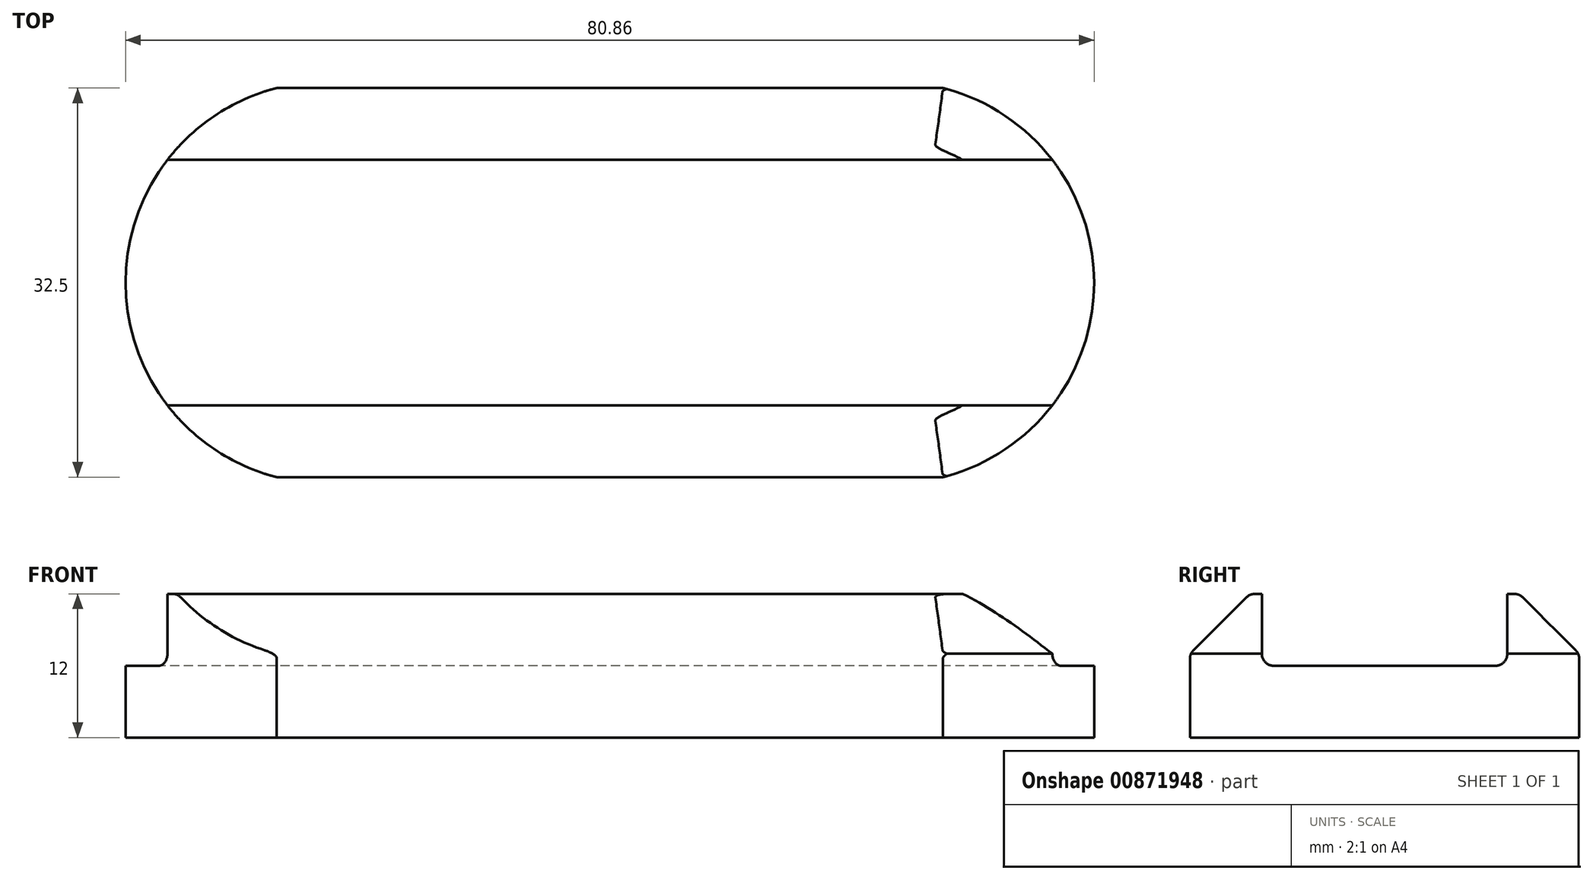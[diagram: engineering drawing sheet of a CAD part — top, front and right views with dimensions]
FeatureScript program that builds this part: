
annotation { "Feature Type Name" : "Feature", "Feature Type Description" : "" }
export const myFeature = defineFeature(function(context is Context, id is Id, definition is map)
    precondition{}
    {
        {
            var Q0;
            Q0=qCreatedBy(makeId("Top.planeOp"),FACE);
            var sketch = newSketch(context, id + "F0", { "sketchPlane" : qUnion([Q0])});
            skLineSegment(sketch, "E0", {"start": v(-30.41, 0) * mm, "end": v(25.96, 0) * mm, "construction": true});
            skLineSegment(sketch, "E1", {"start": v(0, 29.47) * mm, "end": v(0, -28.8) * mm, "construction": true});
            skLineSegment(sketch, "E2.bottom", {"start": v(-36.94, 10.25) * mm, "end": v(36.94, 10.25) * mm});
            skLineSegment(sketch, "E2.top", {"start": v(-36.94, -10.25) * mm, "end": v(36.94, -10.25) * mm});
            skLineSegment(sketch, "E2.left", {"start": v(-27.8, 10.25) * mm, "end": v(-27.8, -10.25) * mm});
            skLineSegment(sketch, "E2.right", {"start": v(27.8, 10.25) * mm, "end": v(27.8, -10.25) * mm});
            skLineSegment(sketch, "E3.bottom", {"start": v(-27.8, 10.25) * mm, "end": v(27.8, 10.25) * mm});
            skLineSegment(sketch, "E3.top", {"start": v(-27.8, 16.25) * mm, "end": v(27.8, 16.25) * mm});
            skLineSegment(sketch, "E3.left", {"start": v(-27.8, 10.25) * mm, "end": v(-27.8, 16.25) * mm});
            skLineSegment(sketch, "E3.right", {"start": v(27.8, 10.25) * mm, "end": v(27.8, 16.25) * mm});
            skLineSegment(sketch, "E4.bottom", {"start": v(-27.8, -10.25) * mm, "end": v(27.8, -10.25) * mm});
            skLineSegment(sketch, "E4.top", {"start": v(-27.8, -16.25) * mm, "end": v(27.8, -16.25) * mm});
            skLineSegment(sketch, "E4.left", {"start": v(-27.8, -10.25) * mm, "end": v(-27.8, -16.25) * mm});
            skLineSegment(sketch, "E4.right", {"start": v(27.8, -10.25) * mm, "end": v(27.8, -16.25) * mm});
            skArc(sketch, "E5", {"start": v(-27.8, -16.25) * mm, "mid": v(-40.43, 0) * mm, "end": v(-27.8, 16.25) * mm});
            skArc(sketch, "E6.MirrorCS", {"start": v(27.8, -16.25) * mm, "mid": v(40.43, 0) * mm, "end": v(27.8, 16.25) * mm});
            skSolve(sketch);
        }
        {
            var Q0;
            {var subQ0=sQuery(id+"F0.wireOp",EDGE,"E3.left");Q0=makeQuery(id+"F0.imprint","IMPRINT",FACE,{"disambiguationData":[TD([[makeQuery(id+"F0.imprint","IMPRINT",EDGE,{"derivedFrom":subQ0}),1.0]])]});}
            var Q1;
            {var subQ0=sQuery(id+"F0.wireOp",EDGE,"E2.left");Q1=makeQuery(id+"F0.imprint","IMPRINT",FACE,{"disambiguationData":[TD([[makeQuery(id+"F0.imprint","IMPRINT",EDGE,{"derivedFrom":subQ0}),-1.0]])]});}
            var Q2;
            {var subQ0=sQuery(id+"F0.wireOp",EDGE,"E4.left");Q2=makeQuery(id+"F0.imprint","IMPRINT",FACE,{"disambiguationData":[TD([[makeQuery(id+"F0.imprint","IMPRINT",EDGE,{"derivedFrom":subQ0}),-1.0]])]});}
            var Q3;
            Q3=makeQuery(id+"F0.imprint","IMPRINT",FACE,{"disambiguationData":[TD([[makeQuery(id+"F0.imprint","IMPRINT",EDGE,{"derivedFrom":sQuery(id+"F0.wireOp",EDGE,"E4.top")}),1.0]])]});
            var Q4;
            {var subQ3=sQuery(id+"F0.wireOp",EDGE,"E3.right");Q4=makeQuery(id+"F0.imprint","IMPRINT",FACE,{"disambiguationData":[TD([[makeQuery(id+"F0.imprint","IMPRINT",EDGE,{"derivedFrom":subQ3}),-1.0]])]});}
            var Q5;
            {var subQ0=sQuery(id+"F0.wireOp",EDGE,"E4.right");Q5=makeQuery(id+"F0.imprint","IMPRINT",FACE,{"disambiguationData":[TD([[makeQuery(id+"F0.imprint","IMPRINT",EDGE,{"derivedFrom":subQ0}),1.0]])]});}
            var Q6;
            Q6=makeQuery(id+"F0.imprint","IMPRINT",FACE,{"disambiguationData":[TD([[makeQuery(id+"F0.imprint","IMPRINT",EDGE,{"derivedFrom":sQuery(id+"F0.wireOp",EDGE,"E3.top")}),-1.0]])]});
            var Q7;
            {var subQ0=sQuery(id+"F0.wireOp",EDGE,"E2.left");Q7=makeQuery(id+"F0.imprint","IMPRINT",FACE,{"disambiguationData":[TD([[makeQuery(id+"F0.imprint","IMPRINT",EDGE,{"derivedFrom":subQ0}),1.0]])]});}
            var Q8;
            {var subQ3=sQuery(id+"F0.wireOp",EDGE,"E2.right");Q8=makeQuery(id+"F0.imprint","IMPRINT",FACE,{"disambiguationData":[TD([[makeQuery(id+"F0.imprint","IMPRINT",EDGE,{"derivedFrom":subQ3}),1.0]])]});}
            extrude(context, id + "F1", {"entities" : qUnion([Q0, Q1, Q2, Q3, Q4, Q5, Q6, Q7, Q8]), "depth" : 6 * mm, "offsetDistance" : 25 * mm});
        }
        {
            var Q0;
            Q0=makeQuery(id+"F0.imprint","IMPRINT",FACE,{"disambiguationData":[TD([[makeQuery(id+"F0.imprint","IMPRINT",EDGE,{"derivedFrom":sQuery(id+"F0.wireOp",EDGE,"E3.top")}),-1.0]])]});
            var Q1;
            {var subQ3=sQuery(id+"F0.wireOp",EDGE,"E3.right");Q1=makeQuery(id+"F0.imprint","IMPRINT",FACE,{"disambiguationData":[TD([[makeQuery(id+"F0.imprint","IMPRINT",EDGE,{"derivedFrom":subQ3}),-1.0]])]});}
            var Q2;
            Q2=makeQuery(id+"F0.imprint","IMPRINT",FACE,{"disambiguationData":[TD([[makeQuery(id+"F0.imprint","IMPRINT",EDGE,{"derivedFrom":sQuery(id+"F0.wireOp",EDGE,"E4.top")}),1.0]])]});
            var Q3;
            {var subQ0=sQuery(id+"F0.wireOp",EDGE,"E4.right");Q3=makeQuery(id+"F0.imprint","IMPRINT",FACE,{"disambiguationData":[TD([[makeQuery(id+"F0.imprint","IMPRINT",EDGE,{"derivedFrom":subQ0}),1.0]])]});}
            var Q4;
            {var subQ0=sQuery(id+"F0.wireOp",EDGE,"E3.left");Q4=makeQuery(id+"F0.imprint","IMPRINT",FACE,{"disambiguationData":[TD([[makeQuery(id+"F0.imprint","IMPRINT",EDGE,{"derivedFrom":subQ0}),1.0]])]});}
            var Q5;
            {var subQ0=sQuery(id+"F0.wireOp",EDGE,"E4.left");Q5=makeQuery(id+"F0.imprint","IMPRINT",FACE,{"disambiguationData":[TD([[makeQuery(id+"F0.imprint","IMPRINT",EDGE,{"derivedFrom":subQ0}),-1.0]])]});}
            extrude(context, id + "F2", {"entities" : qUnion([Q0, Q1, Q2, Q3, Q4, Q5]), "operationType" : NewBodyOperationType.ADD, "depth" : 12 * mm, "offsetDistance" : 25 * mm});
        }
        {
            var Q0;
            Q0=makeQuery(id+"F2.opExtrude","CAP_EDGE",EDGE,{"disambiguationData":[OSD([sQuery(id+"F0.wireOp",EDGE,"E4.top")])],"isStart":false});
            var Q1;
            Q1=makeQuery(id+"F2.opExtrude","CAP_EDGE",EDGE,{"disambiguationData":[OSD([sQuery(id+"F0.wireOp",EDGE,"E3.top")])],"isStart":false});
            chamfer(context, id + "F3", {"entities" : qUnion([Q0, Q1]), "width" : 5 * mm, "tangentPropagation" : true});
        }
        {
            var Q0;
            {var subQ0=sQuery(id+"F0.wireOp",EDGE,"E6.MirrorCS");Q0=makeQuery(id+"F2.opExtrude","CAP_EDGE",EDGE,{"disambiguationData":[OSD([subQ0]),TDD([makeQuery(id+"F0.imprint","IMPRINT",EDGE,{"disambiguationData":[TD([[makeQuery(id+"F0.imprint","INTERSECT",VERTEX,{"derivedFrom":[sQuery(id+"F0.wireOp",EDGE,"E2.bottom"),subQ0]}),-1.0]])],"derivedFrom":subQ0})])],"isStart":false});}
            var Q1;
            {var subQ0=sQuery(id+"F0.wireOp",EDGE,"E6.MirrorCS");Q1=makeQuery(id+"F2.opExtrude","CAP_EDGE",EDGE,{"disambiguationData":[OSD([subQ0]),TDD([makeQuery(id+"F0.imprint","IMPRINT",EDGE,{"disambiguationData":[TD([[makeQuery(id+"F0.imprint","INTERSECT",VERTEX,{"derivedFrom":[sQuery(id+"F0.wireOp",EDGE,"E2.top"),subQ0]}),1.0]])],"derivedFrom":subQ0})])],"isStart":false});}
            var Q2;
            {var subQ0=sQuery(id+"F0.wireOp",EDGE,"E5");Q2=makeQuery(id+"F2.opExtrude","CAP_EDGE",EDGE,{"disambiguationData":[OSD([subQ0]),TDD([makeQuery(id+"F0.imprint","IMPRINT",EDGE,{"disambiguationData":[TD([[makeQuery(id+"F0.imprint","INTERSECT",VERTEX,{"derivedFrom":[sQuery(id+"F0.wireOp",EDGE,"E2.top"),subQ0]}),1.0]])],"derivedFrom":subQ0})])],"isStart":false});}
            var Q3;
            {var subQ0=sQuery(id+"F0.wireOp",EDGE,"E5");Q3=makeQuery(id+"F2.opExtrude","CAP_EDGE",EDGE,{"disambiguationData":[OSD([subQ0]),TDD([makeQuery(id+"F0.imprint","IMPRINT",EDGE,{"disambiguationData":[TD([[makeQuery(id+"F0.imprint","INTERSECT",VERTEX,{"derivedFrom":[sQuery(id+"F0.wireOp",EDGE,"E2.bottom"),subQ0]}),-1.0]])],"derivedFrom":subQ0})])],"isStart":false});}
            chamfer(context, id + "F4", {"entities" : qUnion([Q0, Q1, Q2, Q3]), "width" : 5 * mm, "tangentPropagation" : true});
        }
        {
            var Q0;
            Q0=makeQuery(id+"F2.boolean.opBoolean","INTERSECT",EDGE,{"derivedFrom":[makeQuery(id+"F1.opExtrude","CAP_FACE",FACE,{"disambiguationData":[OSD([sQuery(id+"F0.wireOp",EDGE,"E3.top"),sQuery(id+"F0.wireOp",EDGE,"E4.top"),sQuery(id+"F0.wireOp",EDGE,"E5"),sQuery(id+"F0.wireOp",EDGE,"E6.MirrorCS")])],"isStart":false}),makeQuery(id+"F2.opExtrude","SWEPT_FACE",FACE,{"disambiguationData":[OSD([sQuery(id+"F0.wireOp",EDGE,"E2.top")])]})]});
            var Q1;
            Q1=makeQuery(id+"F2.boolean.opBoolean","INTERSECT",EDGE,{"derivedFrom":[makeQuery(id+"F1.opExtrude","CAP_FACE",FACE,{"disambiguationData":[OSD([sQuery(id+"F0.wireOp",EDGE,"E3.top"),sQuery(id+"F0.wireOp",EDGE,"E4.top"),sQuery(id+"F0.wireOp",EDGE,"E5"),sQuery(id+"F0.wireOp",EDGE,"E6.MirrorCS")])],"isStart":false}),makeQuery(id+"F2.opExtrude","SWEPT_FACE",FACE,{"disambiguationData":[OSD([sQuery(id+"F0.wireOp",EDGE,"E2.bottom")])]})]});
            var Q2;
            {var subQ0=sQuery(id+"F0.wireOp",EDGE,"E3.top");Q2=makeQuery(id+"F3.opChamfer","BLEND_EDGE",EDGE,{"blendedFrom":[makeQuery(id+"F2.opExtrude","CAP_EDGE",EDGE,{"disambiguationData":[OSD([subQ0])],"isStart":false}),makeQuery(id+"F2.opExtrude","CAP_FACE",FACE,{"disambiguationData":[OSD([sQuery(id+"F0.wireOp",EDGE,"E2.bottom"),subQ0,sQuery(id+"F0.wireOp",EDGE,"E5"),sQuery(id+"F0.wireOp",EDGE,"E6.MirrorCS")])],"isStart":false})],"blendedInto":[makeQuery(id+"F2.opExtrude","CAP_FACE",FACE,{"disambiguationData":[OSD([sQuery(id+"F0.wireOp",EDGE,"E2.bottom"),subQ0,sQuery(id+"F0.wireOp",EDGE,"E5"),sQuery(id+"F0.wireOp",EDGE,"E6.MirrorCS")])],"isStart":false})]});}
            var Q3;
            {var subQ0=sQuery(id+"F0.wireOp",EDGE,"E4.top");Q3=makeQuery(id+"F3.opChamfer","BLEND_EDGE",EDGE,{"blendedFrom":[makeQuery(id+"F2.opExtrude","CAP_EDGE",EDGE,{"disambiguationData":[OSD([subQ0])],"isStart":false}),makeQuery(id+"F2.opExtrude","CAP_FACE",FACE,{"disambiguationData":[OSD([sQuery(id+"F0.wireOp",EDGE,"E2.top"),subQ0,sQuery(id+"F0.wireOp",EDGE,"E5"),sQuery(id+"F0.wireOp",EDGE,"E6.MirrorCS")])],"isStart":false})],"blendedInto":[makeQuery(id+"F2.opExtrude","CAP_FACE",FACE,{"disambiguationData":[OSD([sQuery(id+"F0.wireOp",EDGE,"E2.top"),subQ0,sQuery(id+"F0.wireOp",EDGE,"E5"),sQuery(id+"F0.wireOp",EDGE,"E6.MirrorCS")])],"isStart":false})]});}
            var Q4;
            {var subQ0=sQuery(id+"F0.wireOp",EDGE,"E3.top");Q4=makeQuery(id+"F3.opChamfer","BLEND_EDGE",EDGE,{"blendedFrom":[makeQuery(id+"F2.opExtrude","CAP_EDGE",EDGE,{"disambiguationData":[OSD([subQ0])],"isStart":false}),makeQuery(id+"F2.boolean.opBoolean","MERGE",FACE,{"derivedFrom":[makeQuery(id+"F1.opExtrude","SWEPT_FACE",FACE,{"disambiguationData":[OSD([subQ0])]}),makeQuery(id+"F2.opExtrude","SWEPT_FACE",FACE,{"disambiguationData":[OSD([subQ0])]})]})],"blendedInto":[makeQuery(id+"F2.boolean.opBoolean","MERGE",FACE,{"derivedFrom":[makeQuery(id+"F1.opExtrude","SWEPT_FACE",FACE,{"disambiguationData":[OSD([subQ0])]}),makeQuery(id+"F2.opExtrude","SWEPT_FACE",FACE,{"disambiguationData":[OSD([subQ0])]})]})]});}
            var Q5;
            {var subQ0=sQuery(id+"F0.wireOp",EDGE,"E4.top");Q5=makeQuery(id+"F3.opChamfer","BLEND_EDGE",EDGE,{"blendedFrom":[makeQuery(id+"F2.opExtrude","CAP_EDGE",EDGE,{"disambiguationData":[OSD([subQ0])],"isStart":false}),makeQuery(id+"F2.boolean.opBoolean","MERGE",FACE,{"derivedFrom":[makeQuery(id+"F1.opExtrude","SWEPT_FACE",FACE,{"disambiguationData":[OSD([subQ0])]}),makeQuery(id+"F2.opExtrude","SWEPT_FACE",FACE,{"disambiguationData":[OSD([subQ0])]})]})],"blendedInto":[makeQuery(id+"F2.boolean.opBoolean","MERGE",FACE,{"derivedFrom":[makeQuery(id+"F1.opExtrude","SWEPT_FACE",FACE,{"disambiguationData":[OSD([subQ0])]}),makeQuery(id+"F2.opExtrude","SWEPT_FACE",FACE,{"disambiguationData":[OSD([subQ0])]})]})]});}
            fillet(context, id + "F5", {"entities" : qUnion([Q0, Q1, Q2, Q3, Q4, Q5]), "radius" : 1 * mm, "allowEdgeOverflow" : false});
        }
    });
